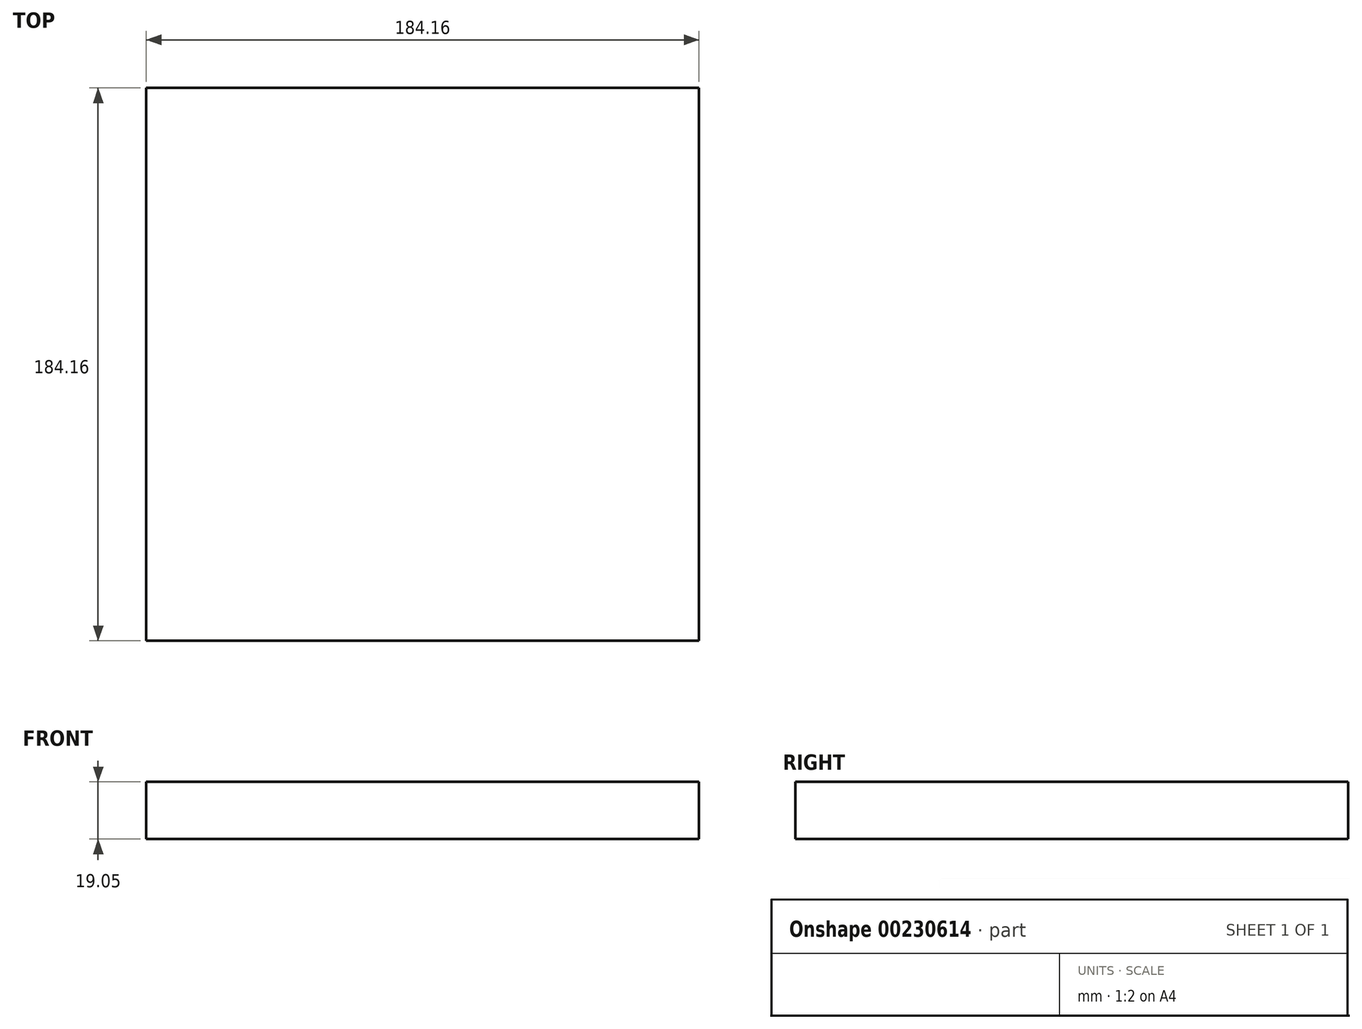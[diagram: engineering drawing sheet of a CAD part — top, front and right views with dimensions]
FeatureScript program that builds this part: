
annotation { "Feature Type Name" : "Feature", "Feature Type Description" : "" }
export const myFeature = defineFeature(function(context is Context, id is Id, definition is map)
    precondition{}
    {
        {
            var Q0;
            Q0=qCreatedBy(makeId("Top.planeOp"),FACE);
            var sketch = newSketch(context, id + "F0", { "sketchPlane" : qUnion([Q0])});
            skLineSegment(sketch, "E0.bottom", {"start": v(92.08, 92.08) * mm, "end": v(-92.07, 92.08) * mm});
            skLineSegment(sketch, "E0.top", {"start": v(92.07, -92.08) * mm, "end": v(-92.08, -92.08) * mm});
            skLineSegment(sketch, "E0.left", {"start": v(92.08, 92.08) * mm, "end": v(92.07, -92.08) * mm});
            skLineSegment(sketch, "E0.right", {"start": v(-92.07, 92.08) * mm, "end": v(-92.08, -92.08) * mm});
            skPoint(sketch, "E0.middle", {"position": v(0, 0) * mm});
            skSolve(sketch);
        }
        {
            var Q0;
            Q0 = qSketchRegion(id + "F0", true);
            extrude(context, id + "F1", {"entities" : qUnion([Q0]), "depth" : 19.05 * mm});
        }
    });
